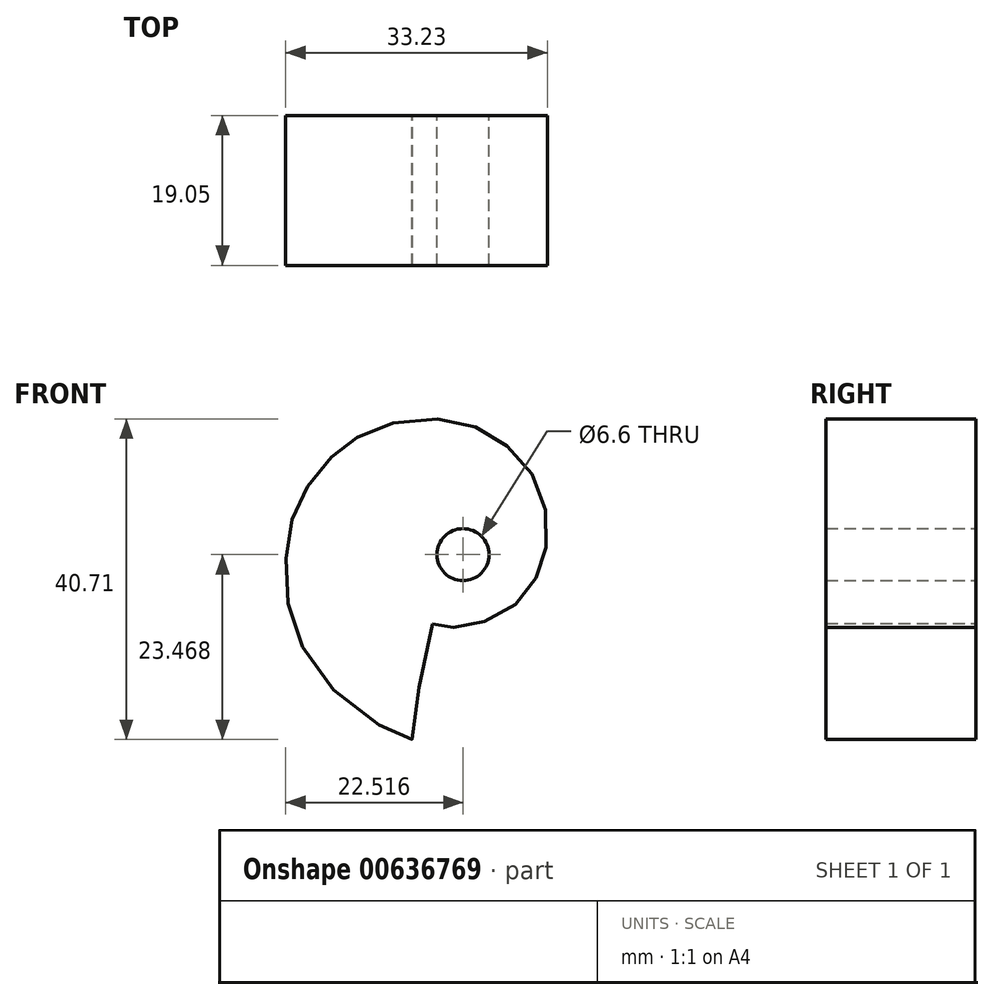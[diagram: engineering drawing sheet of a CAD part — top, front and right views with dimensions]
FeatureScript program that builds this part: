
annotation { "Feature Type Name" : "Feature", "Feature Type Description" : "" }
export const myFeature = defineFeature(function(context is Context, id is Id, definition is map)
    precondition{}
    {
        {
            var Q0;
            Q0=qCreatedBy(makeId("Front.planeOp"),FACE);
            var sketch = newSketch(context, id + "F0", { "sketchPlane" : qUnion([Q0])});
            skFitSpline(sketch, "E0", {"points": [v(-1.64, -9.91) * mm, v(-4.23, -24.52) * mm, v(-4.23, -24.57) * mm, v(-9.56, -22.08) * mm, v(-17.71, -13.68) * mm, v(-20.2, -5.96) * mm, v(-19.91, 1.37) * mm, v(-18.5, 5.96) * mm, v(-15.08, 10.7) * mm, v(-12, 13.33) * mm, v(-7.07, 15.55) * mm, v(0.32, 16) * mm, v(5.42, 14.36) * mm, v(9.57, 11.03) * mm, v(12.28, 6.3) * mm, v(12.85, 0.64) * mm, v(11.78, -3.3) * mm, v(9.53, -6.88) * mm, v(5.42, -9.42) * mm, v(1.72, -10.29) * mm, v(-1.2, -10) * mm, v(-1.64, -9.91) * mm]});
            skCircle(sketch, "E1", {"center": v(2.2, -1.1) * mm, "radius": 3.3 * mm});
            skSolve(sketch);
        }
        {
            var Q0;
            Q0=makeQuery(id+"F0.imprint","IMPRINT",FACE,{"disambiguationData":[TD([[makeQuery(id+"F0.imprint","IMPRINT",EDGE,{"derivedFrom":sQuery(id+"F0.wireOp",EDGE,"E0")}),-1.0]])]});
            extrude(context, id + "F1", {"entities" : qUnion([Q0]), "depth" : 19.05 * mm, "offsetDistance" : 25.4 * mm});
        }
    });
